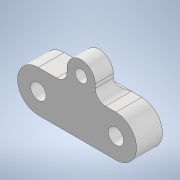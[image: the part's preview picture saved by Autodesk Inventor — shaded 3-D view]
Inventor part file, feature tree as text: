
AUTODESK INVENTOR PART (.ipt)
format: ipt  version: 2020 (Build 240168000, 168)  size: 150,528 bytes
history: native  units: mm
features: other x6, extrude x2, sketch x2, reference x2, thicken_offset x1, fillet x1
ambient origin geometry x8: Origin, YZ Plane, XZ Plane, XY Plane, X Axis, Y Axis, Z Axis, Center Point
bodies: Solid1 (feature_tree)
feature tree (14):
  extrude  "Extrusion1"  Depth=8.0mm
  thicken_offset  "Thicken1"
  extrude  "Extrusion2"  Depth=2.0mm
  fillet  "Fillet1"  Radius=1.5mm
  sketch  "Sketch1"  dims[d0=7.5mm d1=8.0mm]
  reference  "Reference1"
  sketch  "Sketch2"  dims[d2=3.5mm d3=0.0mm d4=1.5mm d5=1.5mm d6=3.5mm d7=0.0mm d8=2.0mm]
  reference  "Reference2"
  parser-record x1  (decoder bookkeeping rows leaked as tree rows — omitted from the tree; the rows remain in map.json)
  other  "delta_1.iam"
  other  "arm_shift_1:2"
  other  "motor_holder_1:1"
  other  "OMRON_ss-5gl:1"
  other  "SS_01GL_E_BASE:1"
note: 1 file-system path scrubbed to <path> (originals preserved in map.json)
